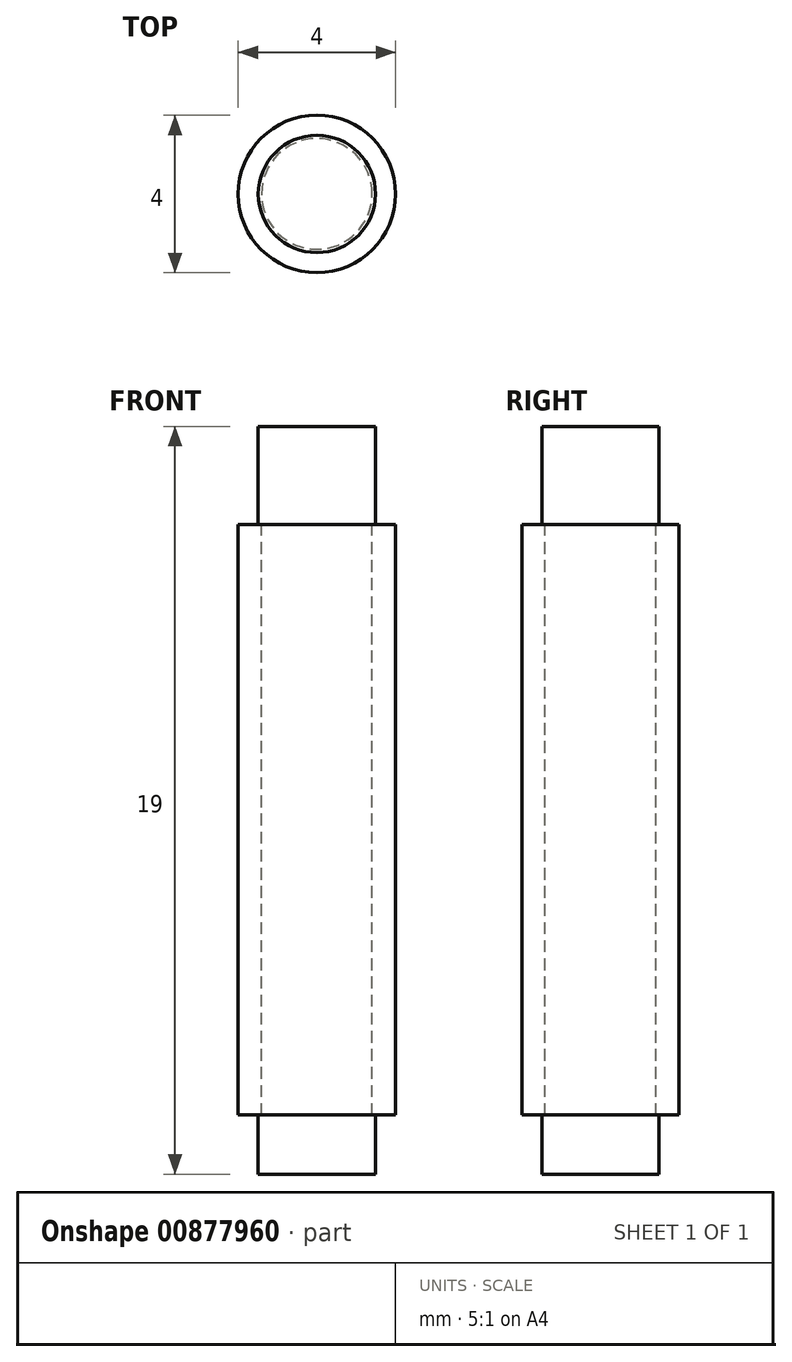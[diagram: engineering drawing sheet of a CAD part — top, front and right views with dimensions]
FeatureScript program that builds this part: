
annotation { "Feature Type Name" : "Feature", "Feature Type Description" : "" }
export const myFeature = defineFeature(function(context is Context, id is Id, definition is map)
    precondition{}
    {
        {
            var Q0;
            Q0=qCreatedBy(makeId("Right.planeOp"),FACE);
            var sketch = newSketch(context, id + "F0", { "sketchPlane" : qUnion([Q0])});
            skLineSegment(sketch, "E0.top", {"start": v(-31.86, 30.06) * mm, "end": v(-33.86, 30.06) * mm});
            skLineSegment(sketch, "E0.left", {"start": v(-31.86, 45.06) * mm, "end": v(-31.86, 30.06) * mm});
            skLineSegment(sketch, "E0.right", {"start": v(-33.86, 45.06) * mm, "end": v(-33.86, 30.06) * mm});
            skLineSegment(sketch, "E1.bottom", {"start": v(-33.35, 45.06) * mm, "end": v(-31.86, 45.06) * mm});
            skLineSegment(sketch, "E1.top", {"start": v(-33.35, 47.56) * mm, "end": v(-31.86, 47.56) * mm});
            skLineSegment(sketch, "E1.left", {"start": v(-33.35, 45.06) * mm, "end": v(-33.35, 47.56) * mm});
            skLineSegment(sketch, "E1.right", {"start": v(-31.86, 45.06) * mm, "end": v(-31.86, 47.56) * mm});
            skLineSegment(sketch, "E2.bottom", {"start": v(-31.86, 30.06) * mm, "end": v(-33.35, 30.06) * mm});
            skLineSegment(sketch, "E2.top", {"start": v(-31.86, 28.56) * mm, "end": v(-33.35, 28.56) * mm});
            skLineSegment(sketch, "E2.left", {"start": v(-31.86, 30.06) * mm, "end": v(-31.86, 28.56) * mm});
            skLineSegment(sketch, "E2.right", {"start": v(-33.35, 30.06) * mm, "end": v(-33.35, 28.56) * mm});
            skLineSegment(sketch, "E3", {"start": v(-31.86, 45.06) * mm, "end": v(-33.86, 45.06) * mm});
            skLineSegment(sketch, "E4", {"start": v(-33.26, 45.06) * mm, "end": v(-33.26, 42.83) * mm});
            skLineSegment(sketch, "E5", {"start": v(-33.26, 42.83) * mm, "end": v(-33.26, 32.33) * mm});
            skLineSegment(sketch, "E6", {"start": v(-33.26, 32.33) * mm, "end": v(-33.26, 30.06) * mm});
            skSolve(sketch);
        }
        {
            var Q0;
            {var subQ4=sQuery(id+"F0.wireOp",EDGE,"E0.top");Q0=makeQuery(id+"F0.imprint","IMPRINT",FACE,{"disambiguationData":[TD([[makeQuery(id+"F0.imprint","IMPRINT",EDGE,{"derivedFrom":subQ4}),-1.0]])]});}
            var Q1;
            Q1=makeQuery(id+"F0.imprint","IMPRINT",FACE,{"disambiguationData":[TD([[makeQuery(id+"F0.imprint","IMPRINT",EDGE,{"derivedFrom":sQuery(id+"F0.wireOp",EDGE,"E1.top")}),-1.0]])]});
            var Q2;
            Q2=makeQuery(id+"F0.imprint","IMPRINT",FACE,{"disambiguationData":[TD([[makeQuery(id+"F0.imprint","IMPRINT",EDGE,{"derivedFrom":sQuery(id+"F0.wireOp",EDGE,"E2.top")}),-1.0]])]});
            var Q3;
            Q3=sQuery(id+"F0.wireOp",EDGE,"E0.left");
            revolve(context, id + "F1", {"surfaceOperationType" : NewSurfaceOperationType.NEW, "entities" : qUnion([Q0, Q1, Q2]), "axis" : qUnion([Q3]), "revolveType" : RevolveType.FULL});
        }
    });
